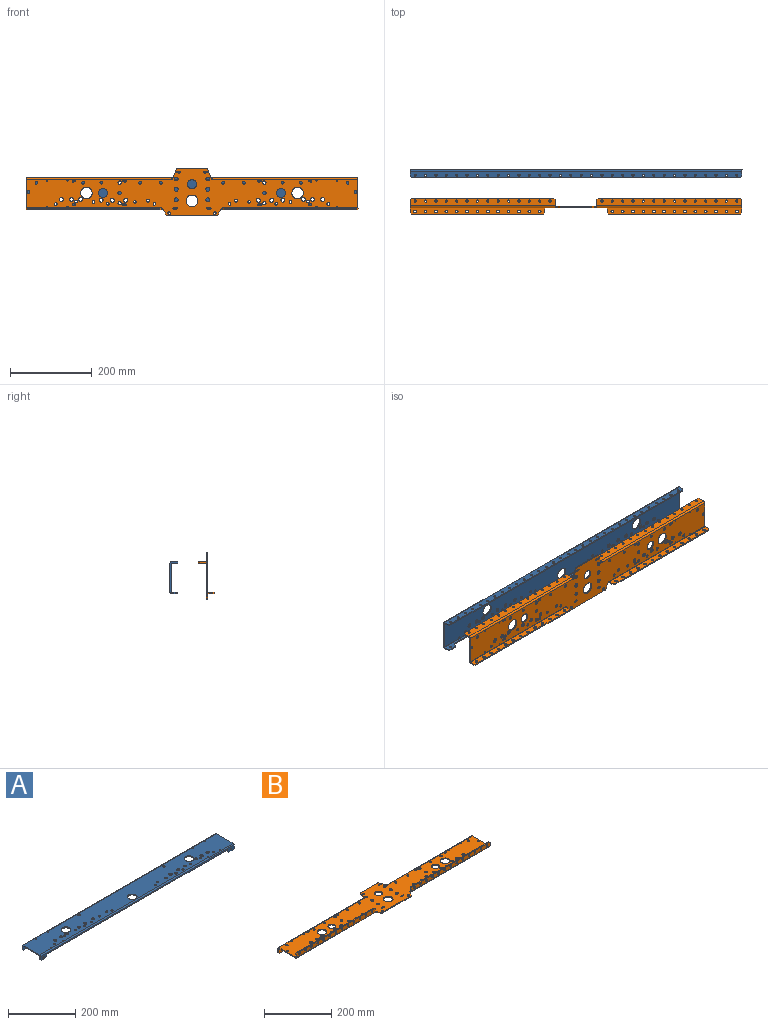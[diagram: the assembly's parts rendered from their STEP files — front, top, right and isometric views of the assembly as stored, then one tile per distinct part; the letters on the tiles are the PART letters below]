
ASSEMBLY  parts=2 mates=1
PART A: 101 faces, bbox 812.8x77.7x19.1 mm
  f0: cylinder r=4.06mm len=8.13mm, axis (0,0,1), area 81.1mm2, adj f83,f84
  f1: cylinder r=4.06mm len=8.13mm, axis (0,0,1), area 81.1mm2, adj f83,f84
  f2: cylinder r=4.06mm len=8.13mm, axis (0,0,1), area 81.1mm2, adj f83,f84
  f3: cylinder r=4.06mm len=8.13mm, axis (0,0,1), area 81.1mm2, adj f83,f84
  f4: cylinder r=3.38mm len=6.76mm, axis (0,0,1), area 67.4mm2, adj f83,f84
  f5: cylinder r=3.38mm len=6.76mm, axis (0,0,1), area 67.4mm2, adj f83,f84
  f6: cylinder r=3.38mm len=6.76mm, axis (0,0,1), area 67.4mm2, adj f83,f84
  f7: cylinder r=3.38mm len=6.76mm, axis (0,0,1), area 67.4mm2, adj f83,f84
  f8: cylinder r=3.35mm len=6.71mm, axis (0,0,1), area 66.9mm2, adj f83,f84
  f9: cylinder r=3.35mm len=6.71mm, axis (0,0,1), area 66.9mm2, adj f83,f84
  f10: cylinder r=3.35mm len=6.71mm, axis (0,0,1), area 66.9mm2, adj f83,f84
  f11: cylinder r=3.35mm len=6.71mm, axis (0,0,1), area 66.9mm2, adj f83,f84
  f12: cylinder r=3.35mm len=6.71mm, axis (0,0,1), area 66.9mm2, adj f83,f84
  f13: cylinder r=3.35mm len=6.71mm, axis (0,0,1), area 66.9mm2, adj f83,f84
  f14: cylinder r=3.35mm len=6.71mm, axis (0,0,1), area 66.9mm2, adj f83,f84
  f15: cylinder r=3.35mm len=6.71mm, axis (0,0,1), area 66.9mm2, adj f83,f84
  f16: cylinder r=3.35mm len=6.71mm, axis (0,0,1), area 66.9mm2, adj f83,f84
  f17: cylinder r=3.35mm len=6.71mm, axis (0,0,1), area 66.9mm2, adj f83,f84
  f18: cylinder r=14.29mm len=28.58mm, axis (0,0,1), area 285mm2, adj f83,f84
  f19: cylinder r=14.29mm len=28.58mm, axis (0,0,1), area 285mm2, adj f83,f84
  f20: cylinder r=1.27mm len=3.18mm, axis (0,0,1), area 25.3mm2, adj f83,f84
  f21: cylinder r=1.27mm len=3.18mm, axis (0,0,1), area 25.3mm2, adj f83,f84
  f22: cylinder r=1.27mm len=3.18mm, axis (0,0,1), area 25.3mm2, adj f83,f84
  f23: cylinder r=1.27mm len=3.18mm, axis (0,0,1), area 25.3mm2, adj f83,f84
  f24: cylinder r=1.27mm len=3.18mm, axis (0,0,1), area 25.3mm2, adj f83,f84
  f25: cylinder r=1.27mm len=3.18mm, axis (0,0,1), area 25.3mm2, adj f83,f84
  f26: cylinder r=1.27mm len=3.18mm, axis (0,0,1), area 25.3mm2, adj f83,f84
  f27: cylinder r=1.27mm len=3.18mm, axis (0,0,1), area 25.3mm2, adj f83,f84
  f28: cylinder r=4.83mm len=9.65mm, axis (0,0,1), area 96.3mm2, adj f83,f84
  f29: cylinder r=4.83mm len=9.65mm, axis (0,0,1), area 96.3mm2, adj f83,f84
  f30: cylinder r=4.83mm len=9.65mm, axis (0,0,1), area 96.3mm2, adj f83,f84
  f31: cylinder r=4.83mm len=9.65mm, axis (0,0,1), area 96.3mm2, adj f83,f84
  f32: cylinder r=4.83mm len=9.65mm, axis (0,0,1), area 96.3mm2, adj f83,f84
  f33: cylinder r=4.83mm len=9.65mm, axis (0,0,1), area 96.3mm2, adj f83,f84
  f34: cylinder r=4.83mm len=9.65mm, axis (0,0,1), area 96.3mm2, adj f83,f84
  f35: cylinder r=4.83mm len=9.65mm, axis (0,0,1), area 96.3mm2, adj f83,f84
  f36: cylinder r=4.83mm len=9.65mm, axis (0,0,1), area 96.3mm2, adj f83,f84
  f37: cylinder r=4.83mm len=9.65mm, axis (0,0,1), area 96.3mm2, adj f83,f84
  f38: cylinder r=4.83mm len=9.65mm, axis (0,0,1), area 96.3mm2, adj f83,f84
  f39: cylinder r=4.83mm len=9.65mm, axis (0,0,1), area 96.3mm2, adj f83,f84
  f40: cylinder r=2.67mm len=5.33mm, axis (0,1,0), area 53.2mm2, adj f75,f76
  f41: cylinder r=2.67mm len=5.33mm, axis (0,1,0), area 53.2mm2, adj f87,f88
  f42: cylinder r=2.67mm len=5.33mm, axis (0,1,0), area 53.2mm2, adj f87,f88
  f43: cylinder r=2.67mm len=5.33mm, axis (0,1,0), area 53.2mm2, adj f87,f88
  f44: cylinder r=2.67mm len=5.33mm, axis (0,1,0), area 53.2mm2, adj f87,f88
  f45: cylinder r=2.67mm len=5.33mm, axis (0,1,0), area 53.2mm2, adj f87,f88
  f46: cylinder r=2.67mm len=5.33mm, axis (0,1,0), area 53.2mm2, adj f87,f88
  f47: cylinder r=2.67mm len=5.33mm, axis (0,1,0), area 53.2mm2, adj f87,f88
  f48: cylinder r=2.67mm len=5.33mm, axis (0,1,0), area 53.2mm2, adj f87,f88
  f49: cylinder r=2.67mm len=5.33mm, axis (0,1,0), area 53.2mm2, adj f87,f88
  f50: cylinder r=2.67mm len=5.33mm, axis (0,1,0), area 53.2mm2, adj f87,f88
  f51: cylinder r=2.67mm len=5.33mm, axis (0,1,0), area 53.2mm2, adj f87,f88
  f52: cylinder r=2.67mm len=5.33mm, axis (0,1,0), area 53.2mm2, adj f87,f88
  f53: cylinder r=2.67mm len=5.33mm, axis (0,1,0), area 53.2mm2, adj f87,f88
  f54: cylinder r=2.67mm len=5.33mm, axis (0,1,0), area 53.2mm2, adj f87,f88
  f55: cylinder r=2.67mm len=5.33mm, axis (0,1,0), area 53.2mm2, adj f87,f88
  f56: cylinder r=2.67mm len=5.33mm, axis (0,1,0), area 53.2mm2, adj f87,f88
  f57: cylinder r=2.67mm len=5.33mm, axis (0,1,0), area 53.2mm2, adj f87,f88
  f58: cylinder r=2.67mm len=5.33mm, axis (0,1,0), area 53.2mm2, adj f87,f88
  f59: cylinder r=2.67mm len=5.33mm, axis (0,1,0), area 53.2mm2, adj f87,f88
  f60: cylinder r=2.67mm len=5.33mm, axis (0,1,0), area 53.2mm2, adj f87,f88
  f61: cylinder r=2.67mm len=5.33mm, axis (0,1,0), area 53.2mm2, adj f87,f88
  f62: cylinder r=2.67mm len=5.33mm, axis (0,1,0), area 53.2mm2, adj f87,f88
  f63: cylinder r=2.67mm len=5.33mm, axis (0,1,0), area 53.2mm2, adj f87,f88
  f64: cylinder r=2.67mm len=5.33mm, axis (0,1,0), area 53.2mm2, adj f87,f88
  f65: cylinder r=2.67mm len=5.33mm, axis (0,1,0), area 53.2mm2, adj f87,f88
  f66: cylinder r=2.67mm len=5.33mm, axis (0,1,0), area 53.2mm2, adj f87,f88
  f67: cylinder r=2.67mm len=5.33mm, axis (0,1,0), area 53.2mm2, adj f87,f88
  f68: cylinder r=2.67mm len=5.33mm, axis (0,1,0), area 53.2mm2, adj f87,f88
  f69: cylinder r=2.67mm len=5.33mm, axis (0,1,0), area 53.2mm2, adj f87,f88
  f70: cylinder r=2.67mm len=5.33mm, axis (0,1,0), area 53.2mm2, adj f87,f88
  f71: cylinder r=2.67mm len=5.33mm, axis (0,1,0), area 53.2mm2, adj f87,f88
  f72: cylinder r=2.67mm len=5.33mm, axis (0,1,0), area 53.2mm2, adj f75,f76
  f73: cylinder r=2.67mm len=5.33mm, axis (0,1,0), area 53.2mm2, adj f87,f88
  f74: cylinder r=14.29mm len=28.58mm, axis (0,0,1), area 285mm2, adj f83,f84
  f75: plane 812.8x15.11mm, normal (0,-1,0), area 3761.3mm2, adj f40,f72,f77,f79,f80,f81,f82,f90
  f76: plane 812.8x15.11mm, normal (0,1,0), area 3761.3mm2, adj f40,f72,f78,f79,f80,f81,f82,f90
  f77: cylinder r=3.94mm len=812.8mm, axis (-1,0,0), area 5026.5mm2, adj f75,f81,f82,f83
  f78: cylinder r=0.76mm len=812.8mm, axis (-1,0,0), area 972.9mm2, adj f76,f81,f82,f84
  f79: plane 19.05x3.18mm, normal (0,0,-1), area 60.5mm2, adj f75,f76,f91,f95
  f80: plane 19.05x3.18mm, normal (0,0,-1), area 60.5mm2, adj f75,f76,f90,f92
  f81: plane 77.72x15.88mm, normal (1,0,0), area 321mm2, adj f75,f76,f77,f78,f83,f84,f85,f86
  f82: plane 77.72x15.88mm, normal (-1,0,0), area 321mm2, adj f75,f76,f77,f78,f83,f84,f85,f86
  f83: plane 812.8x69.85mm, normal (0,0,1), area 53227.5mm2, adj f0,f1,f2,f3,f4,f5,f6,f7
  f84: plane 812.8x69.85mm, normal (0,0,-1), area 53227.5mm2, adj f0,f1,f2,f3,f4,f5,f6,f7
  f85: cylinder r=3.94mm len=812.8mm, axis (1,0,0), area 5026.5mm2, adj f81,f82,f83,f87
  f86: cylinder r=0.76mm len=812.8mm, axis (1,0,0), area 972.9mm2, adj f81,f82,f84,f88
  f87: plane 812.8x15.11mm, normal (0,1,0), area 11558.7mm2, adj f41,f42,f43,f44,f45,f46,f47,f48
  f88: plane 812.8x15.11mm, normal (0,-1,0), area 11558.7mm2, adj f41,f42,f43,f44,f45,f46,f47,f48
  f89: plane 806.45x3.18mm, normal (0,0,-1), area 2560.5mm2, adj f87,f88,f93,f94
  f90: plane 3.18x3.18mm, normal (-0.71,0,-0.71), area 14.3mm2, adj f75,f76,f80,f98
  f91: plane 3.18x3.18mm, normal (0.71,0,-0.71), area 14.3mm2, adj f75,f76,f79,f96
  f92: plane 3.18x3.18mm, normal (0.71,0,-0.71), area 14.3mm2, adj f75,f76,f80,f81
  f93: plane 3.18x3.18mm, normal (0.71,0,-0.71), area 14.3mm2, adj f81,f87,f88,f89
  f94: plane 3.18x3.18mm, normal (-0.71,0,-0.71), area 14.3mm2, adj f82,f87,f88,f89
  f95: plane 3.18x3.18mm, normal (-0.71,0,-0.71), area 14.3mm2, adj f75,f76,f79,f82
  f96: plane 4.76x3.18mm, normal (1,0,0), area 15.1mm2, adj f75,f76,f91,f100
  f97: plane 755.65x3.18mm, normal (0,0,-1), area 2399.2mm2, adj f75,f76,f99,f100
  f98: plane 4.76x3.18mm, normal (-1,0,0), area 15.1mm2, adj f75,f76,f90,f99
  f99: plane 3.18x3.18mm, normal (-0.71,0,-0.71), area 14.3mm2, adj f75,f76,f97,f98
  f100: plane 3.18x3.18mm, normal (0.71,0,-0.71), area 14.3mm2, adj f75,f76,f96,f97
PART B: 198 faces, bbox 812.8x116.3x38.1 mm
  f0: cylinder r=3.35mm len=6.71mm, axis (0,0,1), area 66.9mm2, adj f144,f145
  f1: cylinder r=3.35mm len=6.71mm, axis (0,0,1), area 66.9mm2, adj f144,f145
  f2: cylinder r=3.35mm len=6.71mm, axis (0,0,1), area 66.9mm2, adj f144,f145
  f3: cylinder r=3.35mm len=6.71mm, axis (0,0,1), area 66.9mm2, adj f144,f145
  f4: cylinder r=3.35mm len=6.71mm, axis (0,0,1), area 66.9mm2, adj f144,f145
  f5: cylinder r=3.35mm len=6.71mm, axis (0,0,1), area 66.9mm2, adj f144,f145
  f6: cylinder r=3.35mm len=6.71mm, axis (0,0,1), area 66.9mm2, adj f144,f145
  f7: cylinder r=3.35mm len=6.71mm, axis (0,0,1), area 66.9mm2, adj f144,f145
  f8: cylinder r=3.35mm len=6.71mm, axis (0,0,1), area 66.9mm2, adj f144,f145
  f9: cylinder r=3.35mm len=6.71mm, axis (0,0,1), area 66.9mm2, adj f144,f145
  f10: cylinder r=2.55mm len=5.11mm, axis (0,0,1), area 50.9mm2, adj f144,f145
  f11: cylinder r=1.79mm len=3.57mm, axis (0,0,1), area 35.6mm2, adj f144,f145
  f12: cylinder r=2.55mm len=5.11mm, axis (0,0,1), area 50.9mm2, adj f144,f145
  f13: cylinder r=1.79mm len=3.57mm, axis (0,0,1), area 35.6mm2, adj f144,f145
  f14: cylinder r=14.29mm len=28.58mm, axis (0,0,1), area 285mm2, adj f144,f145
  f15: cylinder r=4.06mm len=8.13mm, axis (0,0,1), area 81.1mm2, adj f144,f145
  f16: cylinder r=1.79mm len=3.57mm, axis (0,0,1), area 35.6mm2, adj f144,f145
  f17: cylinder r=2.55mm len=5.11mm, axis (0,0,1), area 50.9mm2, adj f144,f145
  f18: cylinder r=11.11mm len=22.23mm, axis (0,0,1), area 221.7mm2, adj f144,f145
  f19: cylinder r=4.06mm len=8.13mm, axis (0,0,1), area 81.1mm2, adj f144,f145
  f20: cylinder r=4.06mm len=8.13mm, axis (0,0,1), area 81.1mm2, adj f144,f145
  f21: cylinder r=1.79mm len=3.57mm, axis (0,0,1), area 35.6mm2, adj f144,f145
  f22: cylinder r=2.55mm len=5.11mm, axis (0,0,1), area 50.9mm2, adj f144,f145
  f23: cylinder r=2.55mm len=5.11mm, axis (0,0,1), area 50.9mm2, adj f144,f145
  f24: cylinder r=1.79mm len=3.57mm, axis (0,0,1), area 35.6mm2, adj f144,f145
  f25: cylinder r=2.55mm len=5.11mm, axis (0,0,1), area 50.9mm2, adj f144,f145
  f26: cylinder r=1.79mm len=3.57mm, axis (0,0,1), area 35.6mm2, adj f144,f145
  f27: cylinder r=4.06mm len=8.13mm, axis (0,0,1), area 81.1mm2, adj f144,f145
  f28: cylinder r=4.06mm len=8.13mm, axis (0,0,1), area 81.1mm2, adj f144,f145
  f29: cylinder r=4.06mm len=8.13mm, axis (0,0,1), area 81.1mm2, adj f144,f145
  f30: cylinder r=11.11mm len=22.23mm, axis (0,0,1), area 221.7mm2, adj f144,f145
  f31: cylinder r=1.79mm len=3.57mm, axis (0,0,1), area 35.6mm2, adj f144,f145
  f32: cylinder r=2.55mm len=5.11mm, axis (0,0,1), area 50.9mm2, adj f144,f145
  f33: cylinder r=14.29mm len=28.58mm, axis (0,0,1), area 285mm2, adj f144,f145
  f34: cylinder r=1.79mm len=3.57mm, axis (0,0,1), area 35.6mm2, adj f144,f145
  f35: cylinder r=2.55mm len=5.11mm, axis (0,0,1), area 50.9mm2, adj f144,f145
  f36: cylinder r=3.4mm len=6.81mm, axis (0,0,1), area 67.9mm2, adj f144,f145
  f37: cylinder r=3.4mm len=6.81mm, axis (0,0,1), area 67.9mm2, adj f144,f145
  f38: cylinder r=1.27mm len=3.18mm, axis (0,0,-1), area 25.3mm2, adj f144,f145
  f39: cylinder r=1.27mm len=3.18mm, axis (0,0,-1), area 25.3mm2, adj f144,f145
  f40: cylinder r=1.27mm len=3.18mm, axis (0,0,-1), area 25.3mm2, adj f144,f145
  f41: cylinder r=1.27mm len=3.18mm, axis (0,0,-1), area 25.3mm2, adj f144,f145
  f42: cylinder r=1.27mm len=3.18mm, axis (0,0,-1), area 25.3mm2, adj f144,f145
  f43: cylinder r=1.27mm len=3.18mm, axis (0,0,-1), area 25.3mm2, adj f144,f145
  f44: cylinder r=1.27mm len=3.18mm, axis (0,0,-1), area 25.3mm2, adj f144,f145
  f45: cylinder r=1.27mm len=3.18mm, axis (0,0,-1), area 25.3mm2, adj f144,f145
  f46: cylinder r=3.35mm len=6.71mm, axis (0,0,-1), area 66.9mm2, adj f144,f145
  f47: cylinder r=3.35mm len=6.71mm, axis (0,0,-1), area 66.9mm2, adj f144,f145
  f48: cylinder r=3.35mm len=6.71mm, axis (0,0,-1), area 66.9mm2, adj f144,f145
  f49: cylinder r=3.35mm len=6.71mm, axis (0,0,-1), area 66.9mm2, adj f144,f145
  f50: cylinder r=3.35mm len=6.71mm, axis (0,0,-1), area 66.9mm2, adj f144,f145
  f51: cylinder r=3.35mm len=6.71mm, axis (0,0,-1), area 66.9mm2, adj f144,f145
  f52: cylinder r=3.35mm len=6.71mm, axis (0,0,-1), area 66.9mm2, adj f144,f145
  f53: cylinder r=3.35mm len=6.71mm, axis (0,0,-1), area 66.9mm2, adj f144,f145
  f54: cylinder r=3.35mm len=6.71mm, axis (0,0,-1), area 66.9mm2, adj f144,f145
  f55: cylinder r=3.35mm len=6.71mm, axis (0,0,-1), area 66.9mm2, adj f144,f145
  f56: cylinder r=2.03mm len=4.06mm, axis (0,0,-1), area 40.5mm2, adj f144,f145
  f57: cylinder r=2.03mm len=4.06mm, axis (0,0,-1), area 40.5mm2, adj f144,f145
  f58: cylinder r=2.54mm len=5.08mm, axis (0,0,-1), area 50.7mm2, adj f144,f145
  f59: cylinder r=2.54mm len=5.08mm, axis (0,0,-1), area 50.7mm2, adj f144,f145
  f60: cylinder r=2.03mm len=4.06mm, axis (0,0,-1), area 40.5mm2, adj f144,f145
  f61: cylinder r=2.03mm len=4.06mm, axis (0,0,-1), area 40.5mm2, adj f144,f145
  f62: cylinder r=2.54mm len=5.08mm, axis (0,0,-1), area 50.7mm2, adj f144,f145
  f63: cylinder r=2.54mm len=5.08mm, axis (0,0,-1), area 50.7mm2, adj f144,f145
  f64: cylinder r=4.76mm len=9.53mm, axis (0,0,-1), area 95mm2, adj f144,f145
  f65: cylinder r=4.76mm len=9.53mm, axis (0,0,-1), area 95mm2, adj f144,f145
  f66: cylinder r=4.76mm len=9.53mm, axis (0,0,-1), area 95mm2, adj f144,f145
  f67: cylinder r=4.76mm len=9.53mm, axis (0,0,-1), area 95mm2, adj f144,f145
  f68: cylinder r=4.76mm len=9.53mm, axis (0,0,-1), area 95mm2, adj f144,f145
  f69: cylinder r=4.76mm len=9.53mm, axis (0,0,-1), area 95mm2, adj f144,f145
  f70: cylinder r=11.11mm len=22.23mm, axis (0,0,-1), area 221.7mm2, adj f144,f145
  f71: cylinder r=3.35mm len=6.71mm, axis (0,1,0), area 66.9mm2, adj f166,f167
  f72: cylinder r=3.35mm len=6.71mm, axis (0,1,0), area 66.9mm2, adj f166,f167
  f73: cylinder r=3.35mm len=6.71mm, axis (0,1,0), area 66.9mm2, adj f166,f167
  f74: cylinder r=3.35mm len=6.71mm, axis (0,1,0), area 66.9mm2, adj f166,f167
  f75: cylinder r=3.35mm len=6.71mm, axis (0,1,0), area 66.9mm2, adj f166,f167
  f76: cylinder r=3.35mm len=6.71mm, axis (0,1,0), area 66.9mm2, adj f166,f167
  f77: cylinder r=3.35mm len=6.71mm, axis (0,1,0), area 66.9mm2, adj f166,f167
  f78: cylinder r=3.35mm len=6.71mm, axis (0,1,0), area 66.9mm2, adj f166,f167
  f79: cylinder r=3.35mm len=6.71mm, axis (0,1,0), area 66.9mm2, adj f166,f167
  f80: cylinder r=3.35mm len=6.71mm, axis (0,1,0), area 66.9mm2, adj f166,f167
  f81: cylinder r=3.35mm len=6.71mm, axis (0,1,0), area 66.9mm2, adj f166,f167
  f82: cylinder r=3.35mm len=6.71mm, axis (0,1,0), area 66.9mm2, adj f166,f167
  f83: cylinder r=3.35mm len=6.71mm, axis (0,1,0), area 66.9mm2, adj f166,f167
  f84: cylinder r=3.35mm len=6.71mm, axis (0,1,0), area 66.9mm2, adj f159,f160
  f85: cylinder r=3.35mm len=6.71mm, axis (0,1,0), area 66.9mm2, adj f159,f160
  f86: cylinder r=3.35mm len=6.71mm, axis (0,1,0), area 66.9mm2, adj f159,f160
  f87: cylinder r=3.35mm len=6.71mm, axis (0,1,0), area 66.9mm2, adj f159,f160
  f88: cylinder r=3.35mm len=6.71mm, axis (0,1,0), area 66.9mm2, adj f159,f160
  f89: cylinder r=3.35mm len=6.71mm, axis (0,1,0), area 66.9mm2, adj f159,f160
  f90: cylinder r=3.35mm len=6.71mm, axis (0,1,0), area 66.9mm2, adj f159,f160
  f91: cylinder r=3.35mm len=6.71mm, axis (0,1,0), area 66.9mm2, adj f159,f160
  f92: cylinder r=3.35mm len=6.71mm, axis (0,1,0), area 66.9mm2, adj f159,f160
  f93: cylinder r=3.35mm len=6.71mm, axis (0,1,0), area 66.9mm2, adj f159,f160
  f94: cylinder r=3.35mm len=6.71mm, axis (0,1,0), area 66.9mm2, adj f159,f160
  f95: cylinder r=3.35mm len=6.71mm, axis (0,1,0), area 66.9mm2, adj f159,f160
  f96: cylinder r=3.35mm len=6.71mm, axis (0,1,0), area 66.9mm2, adj f159,f160
  f97: cylinder r=2.67mm len=5.33mm, axis (0,1,0), area 53.2mm2, adj f152,f153
  f98: cylinder r=2.67mm len=5.33mm, axis (0,1,0), area 53.2mm2, adj f152,f153
  f99: cylinder r=2.67mm len=5.33mm, axis (0,1,0), area 53.2mm2, adj f152,f153
  f100: cylinder r=2.67mm len=5.33mm, axis (0,1,0), area 53.2mm2, adj f152,f153
  f101: cylinder r=2.67mm len=5.33mm, axis (0,1,0), area 53.2mm2, adj f152,f153
  f102: cylinder r=2.67mm len=5.33mm, axis (0,1,0), area 53.2mm2, adj f152,f153
  f103: cylinder r=2.67mm len=5.33mm, axis (0,1,0), area 53.2mm2, adj f152,f153
  f104: cylinder r=2.67mm len=5.33mm, axis (0,1,0), area 53.2mm2, adj f152,f153
  f105: cylinder r=2.67mm len=5.33mm, axis (0,1,0), area 53.2mm2, adj f152,f153
  f106: cylinder r=2.67mm len=5.33mm, axis (0,1,0), area 53.2mm2, adj f152,f153
  f107: cylinder r=2.67mm len=5.33mm, axis (0,1,0), area 53.2mm2, adj f152,f153
  f108: cylinder r=2.67mm len=5.33mm, axis (0,1,0), area 53.2mm2, adj f152,f153
  f109: cylinder r=2.67mm len=5.33mm, axis (0,1,0), area 53.2mm2, adj f152,f153
  f110: cylinder r=2.67mm len=5.33mm, axis (0,1,0), area 53.2mm2, adj f152,f153
  f111: cylinder r=2.67mm len=5.33mm, axis (0,1,0), area 53.2mm2, adj f171,f172
  f112: cylinder r=2.67mm len=5.33mm, axis (0,1,0), area 53.2mm2, adj f171,f172
  f113: cylinder r=2.67mm len=5.33mm, axis (0,1,0), area 53.2mm2, adj f171,f172
  f114: cylinder r=2.67mm len=5.33mm, axis (0,1,0), area 53.2mm2, adj f171,f172
  f115: cylinder r=2.67mm len=5.33mm, axis (0,1,0), area 53.2mm2, adj f171,f172
  f116: cylinder r=2.67mm len=5.33mm, axis (0,1,0), area 53.2mm2, adj f171,f172
  f117: cylinder r=2.67mm len=5.33mm, axis (0,1,0), area 53.2mm2, adj f171,f172
  f118: cylinder r=2.67mm len=5.33mm, axis (0,1,0), area 53.2mm2, adj f171,f172
  f119: cylinder r=2.67mm len=5.33mm, axis (0,1,0), area 53.2mm2, adj f171,f172
  f120: cylinder r=2.67mm len=5.33mm, axis (0,1,0), area 53.2mm2, adj f171,f172
  f121: cylinder r=2.67mm len=5.33mm, axis (0,1,0), area 53.2mm2, adj f171,f172
  f122: cylinder r=2.67mm len=5.33mm, axis (0,1,0), area 53.2mm2, adj f171,f172
  f123: cylinder r=2.67mm len=5.33mm, axis (0,1,0), area 53.2mm2, adj f171,f172
  f124: cylinder r=2.67mm len=5.33mm, axis (0,1,0), area 53.2mm2, adj f171,f172
  f125: cylinder r=3.35mm len=6.71mm, axis (0,0,1), area 66.9mm2, adj f144,f145
  f126: cylinder r=3.35mm len=6.71mm, axis (0,0,1), area 66.9mm2, adj f144,f145
  f127: cylinder r=3.35mm len=6.71mm, axis (0,0,1), area 66.9mm2, adj f144,f145
  f128: cylinder r=3.35mm len=6.71mm, axis (0,0,1), area 66.9mm2, adj f144,f145
  f129: cylinder r=3.35mm len=6.71mm, axis (0,0,1), area 66.9mm2, adj f144,f145
  f130: cylinder r=3.35mm len=6.71mm, axis (0,0,1), area 66.9mm2, adj f144,f145
  f131: cylinder r=4.83mm len=9.65mm, axis (0,0,1), area 96.3mm2, adj f144,f145
  f132: cylinder r=4.83mm len=9.65mm, axis (0,0,1), area 96.3mm2, adj f144,f145
  f133: cylinder r=4.83mm len=9.65mm, axis (0,0,1), area 96.3mm2, adj f144,f145
  f134: cylinder r=4.83mm len=9.65mm, axis (0,0,1), area 96.3mm2, adj f144,f145
  f135: cylinder r=4.83mm len=9.65mm, axis (0,0,1), area 96.3mm2, adj f144,f145
  f136: cylinder r=4.83mm len=9.65mm, axis (0,0,1), area 96.3mm2, adj f144,f145
  f137: cylinder r=4.83mm len=9.65mm, axis (0,0,1), area 96.3mm2, adj f144,f145
  f138: cylinder r=4.83mm len=9.65mm, axis (0,0,1), area 96.3mm2, adj f144,f145
  f139: cylinder r=4.83mm len=9.65mm, axis (0,0,1), area 96.3mm2, adj f144,f145
  f140: cylinder r=4.83mm len=9.65mm, axis (0,0,1), area 96.3mm2, adj f144,f145
  f141: cylinder r=4.83mm len=9.65mm, axis (0,0,1), area 96.3mm2, adj f144,f145
  f142: cylinder r=4.83mm len=9.65mm, axis (0,0,1), area 96.3mm2, adj f144,f145
  f143: cylinder r=14.29mm len=28.58mm, axis (0,0,1), area 285mm2, adj f144,f145
  f144: plane 812.8x116.33mm, normal (0,0,1), area 55587.5mm2, adj f0,f1,f2,f3,f4,f5,f6,f7
  f145: plane 812.8x116.33mm, normal (0,0,-1), area 55587.5mm2, adj f0,f1,f2,f3,f4,f5,f6,f7
  f146: plane 71.83x3.18mm, normal (0,1,0), area 228.1mm2, adj f144,f145,f183,f184
  f147: plane 120.39x3.18mm, normal (0,-1,0), area 382.2mm2, adj f144,f145,f187,f189
  f148: plane 3.18x0.91mm, normal (0,1,0), area 2.9mm2, adj f144,f145,f176,f182
  f149: plane 3.18x0.91mm, normal (0,1,0), area 2.9mm2, adj f144,f145,f177,f185
  f150: cylinder r=3.94mm len=355.6mm, axis (1,0,0), area 2199.1mm2, adj f144,f152,f162,f176
  f151: cylinder r=0.76mm len=355.6mm, axis (1,0,0), area 425.6mm2, adj f145,f153,f162,f176
  f152: plane 355.6x18.29mm, normal (0,1,0), area 6180.3mm2, adj f97,f98,f99,f100,f101,f102,f103,f104
  f153: plane 355.6x18.29mm, normal (0,-1,0), area 6180.3mm2, adj f97,f98,f99,f100,f101,f102,f103,f104
  f154: plane 349.25x3.18mm, normal (0,0,-1), area 1108.9mm2, adj f152,f153,f195,f197
  f155: plane 3.18x1.34mm, normal (0,-1,0), area 4.3mm2, adj f144,f145,f174,f188
  f156: plane 3.18x1.34mm, normal (0,-1,0), area 4.3mm2, adj f144,f145,f175,f186
  f157: cylinder r=3.94mm len=330.2mm, axis (1,0,0), area 2042mm2, adj f145,f159,f163,f174
  f158: cylinder r=0.76mm len=330.2mm, axis (1,0,0), area 395.2mm2, adj f144,f160,f163,f174
  f159: plane 330.2x15.11mm, normal (0,-1,0), area 4521.1mm2, adj f84,f85,f86,f87,f88,f89,f90,f91
  f160: plane 330.2x15.11mm, normal (0,1,0), area 4521.1mm2, adj f84,f85,f86,f87,f88,f89,f90,f91
  f161: plane 323.85x3.18mm, normal (0,0,1), area 1028.2mm2, adj f159,f160,f191,f192
  f162: plane 77.72x31.75mm, normal (1,0,0), area 331.1mm2, adj f144,f145,f150,f151,f152,f153,f164,f165
  f163: plane 77.72x31.75mm, normal (-1,0,0), area 331.1mm2, adj f144,f145,f157,f158,f159,f160,f169,f170
  f164: cylinder r=3.94mm len=330.2mm, axis (1,0,0), area 2042mm2, adj f145,f162,f166,f175
  f165: cylinder r=0.76mm len=330.2mm, axis (1,0,0), area 395.2mm2, adj f144,f162,f167,f175
  f166: plane 330.2x15.11mm, normal (0,-1,0), area 4521.1mm2, adj f71,f72,f73,f74,f75,f76,f77,f78
  f167: plane 330.2x15.11mm, normal (0,1,0), area 4521.1mm2, adj f71,f72,f73,f74,f75,f76,f77,f78
  f168: plane 323.85x3.18mm, normal (0,0,1), area 1028.2mm2, adj f166,f167,f193,f194
  f169: cylinder r=3.94mm len=355.6mm, axis (1,0,0), area 2199.1mm2, adj f144,f163,f171,f177
  f170: cylinder r=0.76mm len=355.6mm, axis (1,0,0), area 425.6mm2, adj f145,f163,f172,f177
  f171: plane 355.6x18.29mm, normal (0,1,0), area 6180.3mm2, adj f111,f112,f113,f114,f115,f116,f117,f118
  f172: plane 355.6x18.29mm, normal (0,-1,0), area 6180.3mm2, adj f111,f112,f113,f114,f115,f116,f117,f118
  f173: plane 349.25x3.18mm, normal (0,0,-1), area 1108.9mm2, adj f171,f172,f190,f196
  f174: plane 15.88x3.94mm, normal (1,0,0), area 49.6mm2, adj f155,f157,f158,f159,f160,f192
  f175: plane 15.88x3.94mm, normal (-1,0,0), area 49.6mm2, adj f156,f164,f165,f166,f167,f193
  f176: plane 19.05x3.94mm, normal (-1,0,0), area 59.7mm2, adj f148,f150,f151,f152,f153,f197
  f177: plane 19.05x3.94mm, normal (1,0,0), area 59.7mm2, adj f149,f169,f170,f171,f172,f196
  f178: plane 15.88x9.17mm, normal (0.87,-0.5,0), area 58.2mm2, adj f144,f145,f186,f187
  f179: plane 15.88x9.17mm, normal (-0.87,-0.5,0), area 58.2mm2, adj f144,f145,f188,f189
  f180: plane 23.15x7.97mm, normal (-0.95,0.33,0), area 77.7mm2, adj f144,f145,f184,f185
  f181: plane 23.15x7.97mm, normal (0.95,0.33,0), area 77.7mm2, adj f144,f145,f182,f183
  f182: cylinder r=3.17mm len=3.18mm, axis (0,0,1), area 12.5mm2, adj f144,f145,f148,f181
  f183: cylinder r=3.17mm len=3.18mm, axis (0,0,-1), area 12.5mm2, adj f144,f145,f146,f181
  f184: cylinder r=3.17mm len=3.18mm, axis (0,0,-1), area 12.5mm2, adj f144,f145,f146,f180
  f185: cylinder r=3.17mm len=3.18mm, axis (0,0,-1), area 12.5mm2, adj f144,f145,f149,f180
  f186: cylinder r=3.17mm len=3.18mm, axis (0,0,-1), area 10.6mm2, adj f144,f145,f156,f178
  f187: cylinder r=3.17mm len=3.18mm, axis (0,0,-1), area 10.6mm2, adj f144,f145,f147,f178
  f188: cylinder r=3.17mm len=3.18mm, axis (0,0,1), area 10.6mm2, adj f144,f145,f155,f179
  f189: cylinder r=3.17mm len=3.18mm, axis (0,0,-1), area 10.6mm2, adj f144,f145,f147,f179
  f190: plane 3.18x3.18mm, normal (-0.71,0,-0.71), area 14.3mm2, adj f163,f171,f172,f173
  f191: plane 3.18x3.18mm, normal (-0.71,0,0.71), area 14.3mm2, adj f159,f160,f161,f163
  f192: plane 3.18x3.18mm, normal (0.71,0,0.71), area 14.3mm2, adj f159,f160,f161,f174
  f193: plane 3.18x3.18mm, normal (-0.71,0,0.71), area 14.3mm2, adj f166,f167,f168,f175
  f194: plane 3.18x3.18mm, normal (0.71,0,0.71), area 14.3mm2, adj f162,f166,f167,f168
  f195: plane 3.18x3.18mm, normal (0.71,0,-0.71), area 14.3mm2, adj f152,f153,f154,f162
  f196: plane 3.18x3.18mm, normal (0.71,0,-0.71), area 14.3mm2, adj f171,f172,f173,f177
  f197: plane 3.18x3.18mm, normal (-0.71,0,-0.71), area 14.3mm2, adj f152,f153,f154,f176
PLACE A rot(axis=(0,0.71,0.71),180deg) t=(406.4,-3.18,-17.27)mm
PLACE B rot(axis=(1,0,0),90deg) t=(-406.4,-88.9,-17.27)mm
MATE fastened A.f74 <-> B.f143  axis (0,-1,0) through (0,-3.18,0)mm
